# Revit family: Thorn PIAZZA 3
name_source: partatom
category: Lighting Fixtures
units: mm (PartAtom-declared; Revit-internal decimal feet)

## family parameters
Cut with Voids When Loaded = Yes
Host = Face
Light Source = Yes
Maintain Annotation Orientation = No
Part Type = Normal
Room Calculation Point = Yes
Round Connector Dimension = Use Diameter
Shared = No

## types (5) — shared parameters
Assembly Code = Pr_70_70_48_53
Color Filter = 16777215
Default Elevation = 2000 mm  [stored 6.56168 ft]
Description = Luminaires - wall mounted
Dimming Lamp Color Temperature Shift = <None>
Export Type to IFC As = IfcLightFixtureType
Lamp = LED
Luminaire Height = 306 mm  [stored 1.00394 ft]
Luminaire Length = 195 mm  [stored 0.639764 ft]
Luminaire Width = 383 mm  [stored 1.25656 ft]
Manufacturer = Thorn Lighting
Power Factor = 0.9
Tilt Angle = -90.00°
Type IFC Predefined Type = DIRECTIONSOURCE
Type Image = TLG_PIA3_F_Angled_4000K_2700lm.jpg
URL = https://www.thornlighting.com

## per-type parameters (varying)
| type | Apparent Load | Model | Photometric Web File |
| PIAZZA 3 9-16-27 827-830-840 HF ANT | 23 VA | 96800094 | 96800094_(High4000K).IES |
| PIAZZA 3 9-16-27 827-830-840 HF ANT P | 23 VA | 96800097 | 96800097_(High4000K).IES |
| PIAZZA 3 9-16-27 827-830-840 HF ANT E3 | 26 VA | 96800095 | 96800095_(High4000K).IES |
| PIAZZA 3 9-16-27 827-830-840 HF ANT E3D | 26 VA | 96800096 | 96800096_(High4000K).IES |
| PIAZZA 3 2700 827-830-840 HFIX EC ANT | 23 VA | 96800099 | 96800099_(4000K).IES |

note: [stored X ft] marks values corroborated as IEEE doubles in the binary element streams (Revit-internal decimal feet)

## geometry (parser evidence)
native form markers: Sweep x4
no freeform markers — native parametric forms only
